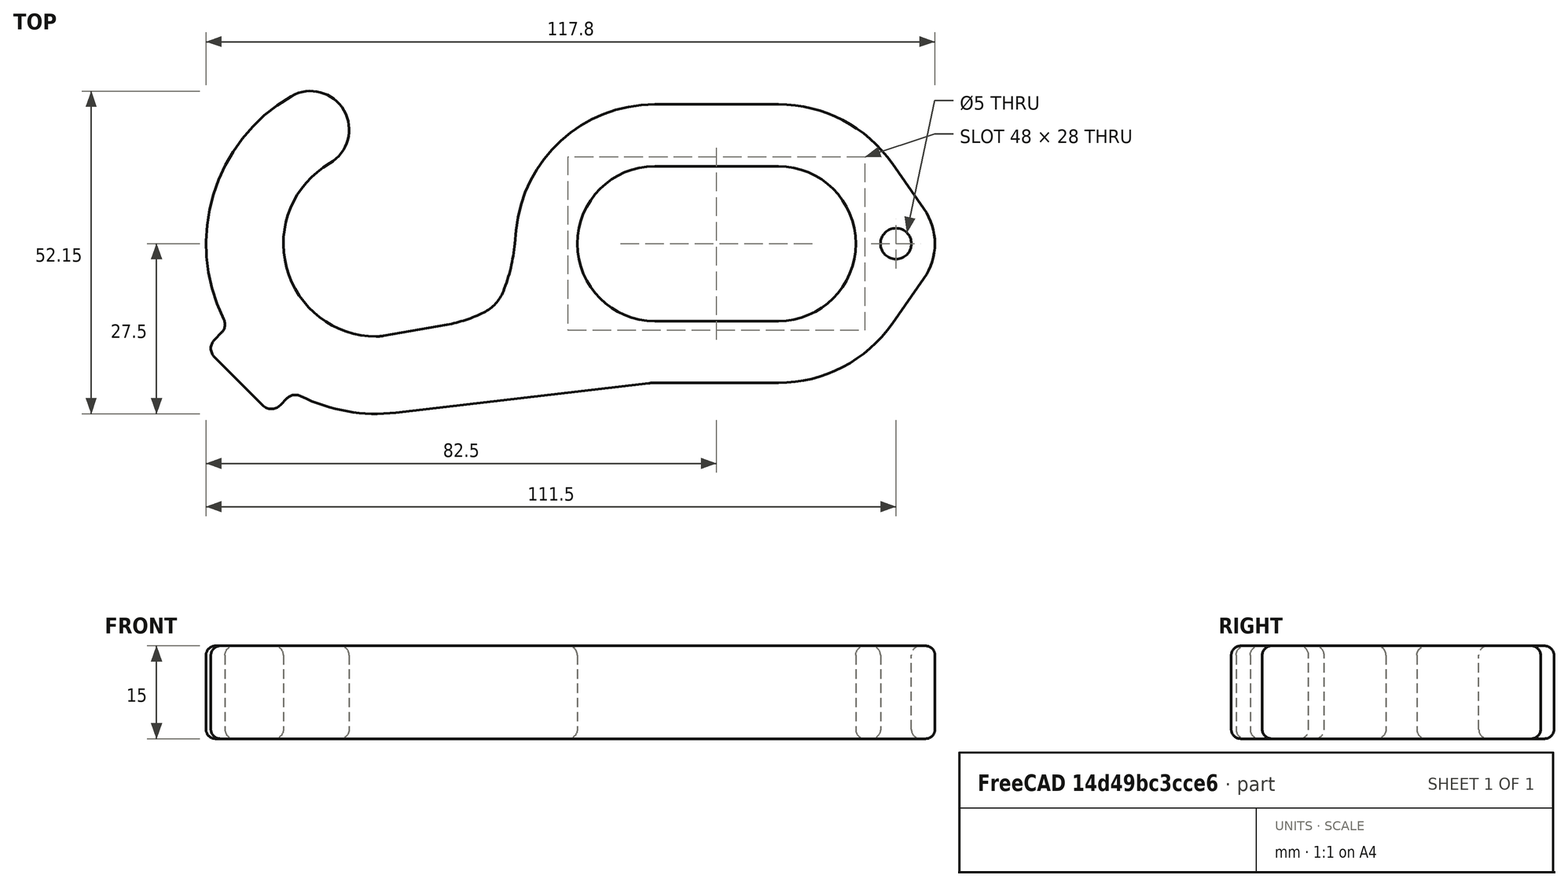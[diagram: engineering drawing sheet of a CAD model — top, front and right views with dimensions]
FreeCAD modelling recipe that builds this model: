
FCSTD DOCUMENT  (FreeCAD 0.18R16146 (Git))
Label: Hook
License: All rights reserved
LicenseURL: http://en.wikipedia.org/wiki/All_rights_reserved
objects: Spreadsheet::Sheet×1, Mesh::Feature×1, App::DocumentObjectGroup×1, Sketcher::SketchObject×1, PartDesign::Pad×1, PartDesign::Fillet×1, PartDesign::Body×1, App::Part×1
note: 5 computed .brp shape members not serialized (recipe doc carries the construction recipe); baked Part::Feature solids carry a one-line shape summary decoded from their .brp

FEATURE [Spreadsheet::Sheet] Spreadsheet  label="pars"
  cells = A1=Bolts and Nuts; B1=Value; D1=Components; E1=Value; A2=Thread Tight Tolerance (Radius, ratio); B2(ThrTighRatio)=0.96; D2=Tight Cilinder Tolerances (Radius, mm); E2(CilTight)=0.1; A3=Thread Tight Tolerance (Radius, mm); B3(ThrTightmm)=0.1; D3=Loose Cilinder Tolerances (Radius, mm); E3(CilLoose)=0.1; A5=Nut Slot Width Clearance (mm); B5(NutWidthClearmm)=0.1; A6=Nut Slot Thickess Clearance (mm); B6(NutThickClearmm)=0.1; A13=Particular parameters; B13=Value
FEATURE [Mesh::Feature] Easy_Grip_NoTouch_Door_Opener_V3_notext
FEATURE [App::DocumentObjectGroup] Group  label="Reference"
  Group = -> [Easy_Grip_NoTouch_Door_Opener_V3_notext]
FEATURE [Sketcher::SketchObject] Sketch  label="Base"
  MapMode = 5
  Support = -> [XY_Plane001]
  sketch-geometry (34):
    g0: ArcOfCircle CenterX=0 CenterY=0 CenterZ=0 NormalX=0 NormalY=0 NormalZ=1 AngleXU=0 Radius=12.5 StartAngle=1.5708 EndAngle=4.71239
    g1: ArcOfCircle CenterX=20 CenterY=0 CenterZ=0 NormalX=0 NormalY=0 NormalZ=1 AngleXU=0 Radius=12.5 StartAngle=4.71239 EndAngle=7.85398
    g2: LineSegment StartX=-2.3e-15 StartY=-12.5 StartZ=0 EndX=20 EndY=-12.5 EndZ=0
    g3: LineSegment StartX=-2e-15 StartY=12.5 StartZ=0 EndX=20 EndY=12.5 EndZ=0
    g4: ArcOfCircle CenterX=0 CenterY=0 CenterZ=0 NormalX=0 NormalY=0 NormalZ=1 AngleXU=0 Radius=22.5 StartAngle=1.5708 EndAngle=3.04677
    g5: ArcOfCircle CenterX=20 CenterY=0 CenterZ=0 NormalX=0 NormalY=0 NormalZ=1 AngleXU=0 Radius=22.5 StartAngle=0.610865 EndAngle=1.5708
    g6: ArcOfCircle CenterX=35.5038 CenterY=0 CenterZ=0 NormalX=0 NormalY=0 NormalZ=1 AngleXU=0 Radius=9.8 StartAngle=5.67232 EndAngle=6.89405
    g7: ArcOfCircle CenterX=20 CenterY=0 CenterZ=0 NormalX=0 NormalY=0 NormalZ=1 AngleXU=0 Radius=22.5 StartAngle=4.71239 EndAngle=5.67232
    g8: LineSegment StartX=38.4309 StartY=12.9055 StartZ=0 EndX=43.5315 EndY=5.62105 EndZ=0
    g9: LineSegment StartX=43.5315 StartY=-5.62105 StartZ=0 EndX=38.4309 EndY=-12.9055 EndZ=0
    g10: Circle CenterX=39 CenterY=0 CenterZ=0 NormalX=0 NormalY=0 NormalZ=1 AngleXU=0 Radius=2.5
    g11: LineSegment StartX=-2.8e-15 StartY=22.5 StartZ=0 EndX=20 EndY=22.5 EndZ=0
    g12: LineSegment StartX=5e-16 StartY=-22.5 StartZ=0 EndX=20 EndY=-22.5 EndZ=0
    g13: ArcOfCircle CenterX=0 CenterY=-30.5 CenterZ=0 NormalX=0 NormalY=0 NormalZ=1 AngleXU=0 Radius=8 StartAngle=1.5708 EndAngle=1.68672
    g14: LineSegment StartX=-41.8194 StartY=-27.3154 StartZ=0 EndX=-0.925278 EndY=-22.5537 EndZ=0
    g15: ArcOfCircle CenterX=-45 CenterY=0 CenterZ=0 NormalX=0 NormalY=0 NormalZ=1 AngleXU=0 Radius=15 StartAngle=2.0944 EndAngle=4.71239
    g16: ArcOfCircle CenterX=-55.625 CenterY=18.403 CenterZ=0 NormalX=0 NormalY=0 NormalZ=1 AngleXU=0 Radius=6.25 StartAngle=5.23599 EndAngle=8.37758
    g17: ArcOfCircle CenterX=-45 CenterY=0 CenterZ=0 NormalX=0 NormalY=0 NormalZ=1 AngleXU=0 Radius=27.5 StartAngle=2.0944 EndAngle=3.60155
    g18: ArcOfCircle CenterX=-45 CenterY=0 CenterZ=0 NormalX=0 NormalY=0 NormalZ=1 AngleXU=0 Radius=27.5 StartAngle=4.25243 EndAngle=4.82831
    g19: ArcOfCircle CenterX=-58.0509 CenterY=-26.3445 CenterZ=0 NormalX=0 NormalY=0 NormalZ=1 AngleXU=0 Radius=1.9 StartAngle=1.11084 EndAngle=2.35619
    g20: ArcOfCircle CenterX=-61.94 CenterY=-24.7182 CenterZ=0 NormalX=0 NormalY=0 NormalZ=1 AngleXU=0 Radius=2 StartAngle=3.92699 EndAngle=5.49779
    g21: ArcOfCircle CenterX=-69.7182 CenterY=-16.94 CenterZ=0 NormalX=0 NormalY=0 NormalZ=1 AngleXU=0 Radius=2 StartAngle=2.35619 EndAngle=3.92699
    g22: ArcOfCircle CenterX=-71.3445 CenterY=-13.0509 CenterZ=0 NormalX=0 NormalY=0 NormalZ=1 AngleXU=0 Radius=1.9 StartAngle=5.49779 EndAngle=6.74314
    g23: LineSegment StartX=-71.1324 StartY=-15.5258 StartZ=0 EndX=-70.001 EndY=-14.3944 EndZ=0
    g24: LineSegment StartX=-71.1324 StartY=-18.3542 StartZ=0 EndX=-63.3542 EndY=-26.1324 EndZ=0
    g25: LineSegment StartX=-60.5258 StartY=-26.1324 StartZ=0 EndX=-59.3944 EndY=-25.001 EndZ=0
    g26: LineSegment [constr] StartX=-55.625 StartY=18.403 StartZ=0 EndX=-45 EndY=0 EndZ=0
    g27: ArcOfCircle CenterX=-45 CenterY=-8 CenterZ=0 NormalX=0 NormalY=0 NormalZ=1 AngleXU=0 Radius=7 StartAngle=4.71239 EndAngle=4.88692
    g28: LineSegment StartX=-43.7845 StartY=-14.8937 StartZ=0 EndX=-33.6046 EndY=-13.0987 EndZ=0
    g29: LineSegment StartX=-22.3989 StartY=2.13032 StartZ=0 EndX=-22.6015 EndY=8.9e-15 EndZ=0
    g30: LineSegment [constr] StartX=-45 StartY=0 StartZ=0 EndX=-45 EndY=-15 EndZ=0
    g31: ArcOfCircle CenterX=-37.4248 CenterY=8.5671 CenterZ=0 NormalX=0 NormalY=0 NormalZ=1 AngleXU=0 Radius=22 StartAngle=4.88692 EndAngle=5.17553
    g32: ArcOfCircle CenterX=-30.5 CenterY=-5.3 CenterZ=0 NormalX=0 NormalY=0 NormalZ=1 AngleXU=0 Radius=6.5 StartAngle=5.17553 EndAngle=5.90437
    g33: ArcOfCircle CenterX=-50.4757 CenterY=2.65107 CenterZ=0 NormalX=0 NormalY=0 NormalZ=1 AngleXU=0 Radius=28 StartAngle=5.90437 EndAngle=6.18836
  constraints (83):
    c: Tangent(g0,g3) = 1.5708
    c: Tangent(g0,g2) = -1.5708
    c: Tangent(g2,g1) = -1.5708
    c: Tangent(g3,g1) = 1.5708
    c: Horizontal(g2)
    c: Equal(g0,g1)
    c: Coincident(g0,g-1)
    c: Radius(g0) = 12.5
    c: DistanceX(g0,g1) = 20
    c: Coincident(g0,g4)
    c: Coincident(g1,g5)
    c: Coincident(g1,g7)
    c: Equal(g5,g7)
    c: Tangent(g5,g8) = 1.5708
    c: Tangent(g6,g8) = 1.5708
    c: Tangent(g6,g9) = 1.5708
    c: Tangent(g7,g9) = 1.5708
    c: PointOnObject(g6,g-1)
    c: Radius(g5) = 22.5
    c: Equal(g4,g5)
    c: Angle(g8) = -0.959931
    c: Radius(g6) = 9.8
    c: PointOnObject(g10,g-1)
    c: Radius(g10) = 2.5
    c: DistanceX(g10) = 39
    c: Tangent(g4,g11) = 1.5708
    c: Tangent(g5,g11) = 1.5708
    c: Horizontal(g12)
    c: Tangent(g12,g13) = 1.5708
    c: Tangent(g13,g14) = 1.5708
    c: PointOnObject(g18,g-1)
    c: Coincident(g15,g17)
    c: Coincident(g15,g18)
    c: Tangent(g14,g18) = -1.5708
    c: Tangent(g16,g17) = -1.5708
    c: Tangent(g15,g16) = 1.5708
    c: Radius(g15) = 15
    c: DistanceX(g15) = -45
    c: Radius(g17) = 27.5
    c: Equal(g17,g18)
    c: Tangent(g17,g22) = 1.5708
    c: Tangent(g22,g23) = -1.5708
    c: Tangent(g21,g23) = 1.5708
    c: Tangent(g21,g24) = -1.5708
    c: Tangent(g20,g24) = -1.5708
    c: Tangent(g20,g25) = -1.5708
    c: Tangent(g19,g25) = 1.5708
    c: Tangent(g18,g19) = 1.5708
    c: Angle(g25) = 0.785398
    c: Radius(g19) = 1.9
    c: Equal(g22,g19)
    c: Perpendicular(g25,g24)
    c: Perpendicular(g24,g23)
    c: Radius(g21) = 2
    c: Equal(g21,g20)
    c: Distance(g21,g20) = 15
    c: Distance(g25) = 1.6
    c: Equal(g23,g25)
    c: Coincident(g16,g26)
    c: Coincident(g15,g26)
    c: Angle(g-1,g26) = 2.0944
    c: Angle(g28) = 0.174533
    c: Tangent(g15,g27) = -1.5708
    c: Tangent(g27,g28) = -1.5708
    c: Tangent(g4,g29) = -1.5708
    c: Vertical(g30)
    c: Coincident(g15,g30)
    c: Coincident(g30,g15)
    c: Radius(g27) = 7
    c: Coincident(g31,g32)
    c: Tangent(g29,g33) = 1.5708
    c: Tangent(g32,g33) = -1.5708
    c: Tangent(g28,g31) = -1.5708
    c: Tangent(g31,g32)
    c: Radius(g32) = 6.5
    c: PointOnObject(g29,g-1)
    c: Radius(g31) = 22
    c: Radius(g33) = 28
    c: DistanceX(g32) = -30.5
    c: DistanceY(g32) = -5.3
    c: Tangent(g7,g12) = -1.5708
    c: PointOnObject(g13,g-2)
    c: Radius(g13) = 8
FEATURE [PartDesign::Pad] Pad  label="Base001"
  Length = 15
  Length2 = 100
  Profile = -> Sketch
  Type = 0
FEATURE [PartDesign::Fillet] Fillet  label="TotalFillet"
  Base = -> Pad [Edge85,Edge64,Edge63,Edge96,Edge90,Edge95]
  BaseFeature = -> Pad
  Radius = 1.5
FEATURE [PartDesign::Body] Body
  Group = -> [Sketch,Pad,Fillet]
  Origin = -> Origin001
  Tip = -> Fillet
FEATURE [App::Part] Part  label="Hook"
  Group = -> [Body]
  Origin = -> Origin
